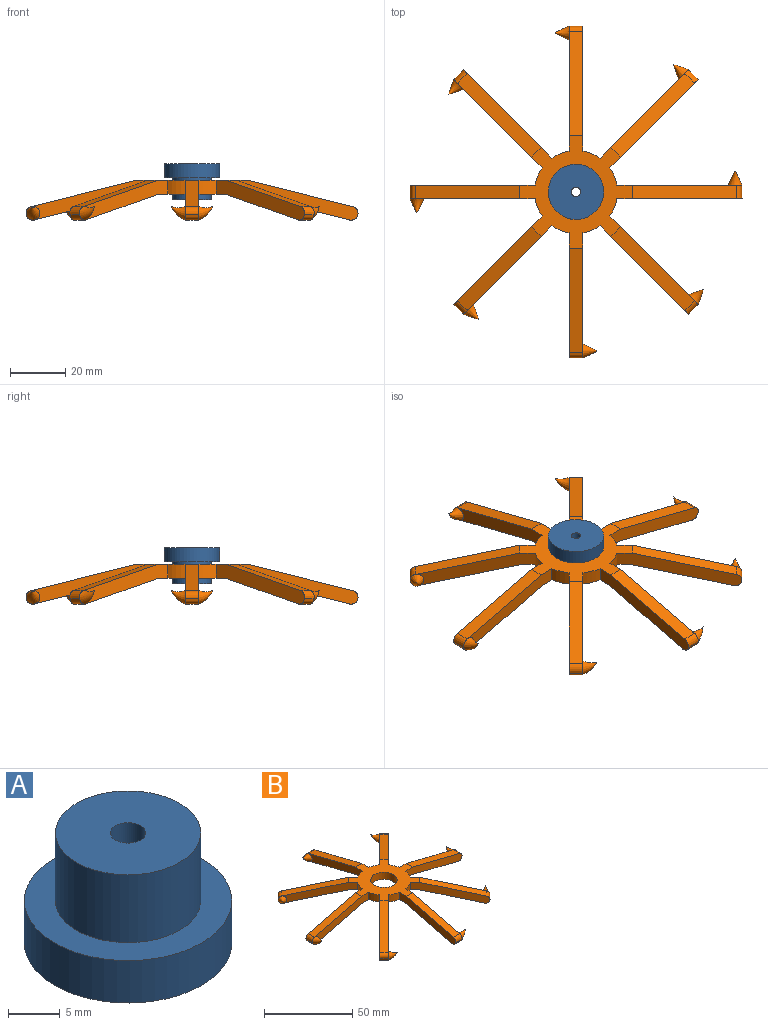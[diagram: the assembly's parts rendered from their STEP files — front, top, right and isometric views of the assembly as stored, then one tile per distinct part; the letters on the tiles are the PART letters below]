
ASSEMBLY  parts=2 mates=1
PART A: 6 faces, bbox 20x20x13 mm
  f0: cylinder r=10mm len=20mm, axis (0,0,-1), area 314.2mm2, adj f1,f2
  f1: plane 20x20mm, normal (0,0,1), area 160.2mm2, adj f0,f3
  f2: plane 20x20mm, normal (0,0,-1), area 305.1mm2, adj f0,f5
  f3: cylinder r=7mm len=14mm, axis (0,0,-1), area 351.9mm2, adj f1,f4
  f4: plane 14x14mm, normal (0,0,1), area 144.9mm2, adj f3,f5
  f5: cylinder r=1.7mm len=13mm, axis (0,0,-1), area 138.9mm2, adj f2,f4
PART B: 67 faces, bbox 120.2x120.2x14.4 mm
  f0: plane 45.28x14.39mm, normal (0,-1,0), area 229.5mm2, adj f2,f3,f4,f5,f7,f8,f10
  f1: plane 43.39x14.32mm, normal (0,1,0), area 209.9mm2, adj f2,f3,f4,f5,f6,f18
  f2: plane 37.88x9.47mm, normal (0.24,0,0.97), area 195.2mm2, adj f0,f1,f5,f8
  f3: plane 37.28x9.32mm, normal (-0.24,0,-0.97), area 192.1mm2, adj f0,f1,f4,f7
  f4: plane 39.38x39.38mm, normal (0,0,-1), area 720.6mm2, adj f0,f1,f3,f9,f10,f11,f12,f14
  f5: plane 40.62x40.62mm, normal (0,0,1), area 745.2mm2, adj f0,f1,f2,f9,f10,f11,f12,f13
  f6: bspline ~5x5mm, area 48.7mm2, adj f1,f7,f8
  f7: extruded ~5x3.03mm, area 19.6mm2, adj f0,f3,f6,f8
  f8: extruded ~5x3.03mm, area 19.6mm2, adj f0,f2,f6,f7
  f9: cylinder r=7.5mm len=15mm, axis (0,0,1), area 235.6mm2, adj f4,f5
  f10: cylinder r=15mm len=6.19mm, axis (0,0,1), area 33.8mm2, adj f0,f4,f5,f60
  f11: plane 32.02x32.02mm, normal (0.71,-0.71,0), area 229.5mm2, adj f4,f5,f13,f14,f16,f17,f18
  f12: plane 30.68x30.68mm, normal (-0.71,0.71,0), area 209.9mm2, adj f4,f5,f13,f14,f15,f26
  f13: plane 30.32x30.32mm, normal (0.17,0.17,0.97), area 195.2mm2, adj f5,f11,f12,f17
  f14: plane 29.9x29.89mm, normal (-0.17,-0.17,-0.97), area 192.1mm2, adj f4,f11,f12,f16
  f15: bspline ~5.3x5.3mm, area 48.7mm2, adj f12,f16,f17
  f16: extruded ~5.68x5.68mm, area 19.6mm2, adj f11,f14,f15,f17
  f17: extruded ~4.87x4.87mm, area 19.6mm2, adj f11,f13,f15,f16
  f18: cylinder r=15mm len=6.19mm, axis (0,0,1), area 33.8mm2, adj f1,f4,f5,f11
  f19: plane 45.28x14.39mm, normal (1,0,0), area 229.5mm2, adj f4,f5,f21,f22,f24,f25,f26
  f20: plane 43.39x14.32mm, normal (-1,0,0), area 209.9mm2, adj f4,f5,f21,f22,f23,f34
  f21: plane 37.88x9.47mm, normal (0,0.24,0.97), area 195.2mm2, adj f5,f19,f20,f25
  f22: plane 37.28x9.32mm, normal (0,-0.24,-0.97), area 192.1mm2, adj f4,f19,f20,f24
  f23: bspline ~5x5mm, area 48.7mm2, adj f20,f24,f25
  f24: extruded ~5x3.03mm, area 19.6mm2, adj f19,f22,f23,f25
  f25: extruded ~5x3.03mm, area 19.6mm2, adj f19,f21,f23,f24
  f26: cylinder r=15mm len=6.19mm, axis (0,0,1), area 33.8mm2, adj f4,f5,f12,f19
  f27: plane 32.02x32.02mm, normal (0.71,0.71,0), area 229.5mm2, adj f4,f5,f29,f30,f32,f33,f34
  f28: plane 30.68x30.68mm, normal (-0.71,-0.71,0), area 209.9mm2, adj f4,f5,f29,f30,f31,f42
  f29: plane 30.32x30.32mm, normal (-0.17,0.17,0.97), area 195.2mm2, adj f5,f27,f28,f33
  f30: plane 29.9x29.89mm, normal (0.17,-0.17,-0.97), area 192.1mm2, adj f4,f27,f28,f32
  f31: bspline ~5.3x5.3mm, area 48.7mm2, adj f28,f32,f33
  f32: extruded ~5.68x5.68mm, area 19.6mm2, adj f27,f30,f31,f33
  f33: extruded ~4.87x4.87mm, area 19.6mm2, adj f27,f29,f31,f32
  f34: cylinder r=15mm len=6.19mm, axis (0,0,1), area 33.8mm2, adj f4,f5,f20,f27
  f35: plane 45.28x14.39mm, normal (0,1,0), area 229.5mm2, adj f4,f5,f37,f38,f40,f41,f42
  f36: plane 43.39x14.32mm, normal (0,-1,0), area 209.9mm2, adj f4,f5,f37,f38,f39,f50
  f37: plane 37.88x9.47mm, normal (-0.24,0,0.97), area 195.2mm2, adj f5,f35,f36,f41
  f38: plane 37.28x9.32mm, normal (0.24,0,-0.97), area 192.1mm2, adj f4,f35,f36,f40
  f39: bspline ~5x5mm, area 48.7mm2, adj f36,f40,f41
  f40: extruded ~5x3.03mm, area 19.6mm2, adj f35,f38,f39,f41
  f41: extruded ~5x3.03mm, area 19.6mm2, adj f35,f37,f39,f40
  f42: cylinder r=15mm len=6.19mm, axis (0,0,1), area 33.8mm2, adj f4,f5,f28,f35
  f43: plane 32.02x32.02mm, normal (-0.71,0.71,0), area 229.5mm2, adj f4,f5,f45,f46,f48,f49,f50
  f44: plane 30.68x30.68mm, normal (0.71,-0.71,0), area 209.9mm2, adj f4,f5,f45,f46,f47,f58
  f45: plane 30.32x30.32mm, normal (-0.17,-0.17,0.97), area 195.2mm2, adj f5,f43,f44,f49
  f46: plane 29.9x29.89mm, normal (0.17,0.17,-0.97), area 192.1mm2, adj f4,f43,f44,f48
  f47: bspline ~5.3x5.3mm, area 48.7mm2, adj f44,f48,f49
  f48: extruded ~5.68x5.68mm, area 19.6mm2, adj f43,f46,f47,f49
  f49: extruded ~4.87x4.87mm, area 19.6mm2, adj f43,f45,f47,f48
  f50: cylinder r=15mm len=6.19mm, axis (0,0,1), area 33.8mm2, adj f4,f5,f36,f43
  f51: plane 45.28x14.39mm, normal (-1,0,0), area 229.5mm2, adj f4,f5,f53,f54,f56,f57,f58
  f52: plane 43.39x14.32mm, normal (1,0,0), area 209.9mm2, adj f4,f5,f53,f54,f55,f66
  f53: plane 37.88x9.47mm, normal (0,-0.24,0.97), area 195.2mm2, adj f5,f51,f52,f57
  f54: plane 37.28x9.32mm, normal (0,0.24,-0.97), area 192.1mm2, adj f4,f51,f52,f56
  f55: bspline ~5x5mm, area 48.7mm2, adj f52,f56,f57
  f56: extruded ~5x3.03mm, area 19.6mm2, adj f51,f54,f55,f57
  f57: extruded ~5x3.03mm, area 19.6mm2, adj f51,f53,f55,f56
  f58: cylinder r=15mm len=6.19mm, axis (0,0,1), area 33.8mm2, adj f4,f5,f44,f51
  f59: plane 32.02x32.02mm, normal (-0.71,-0.71,0), area 229.5mm2, adj f4,f5,f61,f62,f64,f65,f66
  f60: plane 30.68x30.68mm, normal (0.71,0.71,0), area 209.9mm2, adj f4,f5,f10,f61,f62,f63
  f61: plane 30.32x30.32mm, normal (0.17,-0.17,0.97), area 195.2mm2, adj f5,f59,f60,f65
  f62: plane 29.9x29.89mm, normal (-0.17,0.17,-0.97), area 192.1mm2, adj f4,f59,f60,f64
  f63: bspline ~5.3x5.3mm, area 48.7mm2, adj f60,f64,f65
  f64: extruded ~5.68x5.68mm, area 19.6mm2, adj f59,f62,f63,f65
  f65: extruded ~4.87x4.87mm, area 19.6mm2, adj f59,f61,f63,f64
  f66: cylinder r=15mm len=6.19mm, axis (0,0,1), area 33.8mm2, adj f4,f5,f52,f59
PLACE A rot(axis=(1,0,0),180deg) t=(0,0,6)mm
PLACE B t=(0,0,-2.5)mm
MATE fastened B.f9 <-> A.f0  axis (0,0,1) through (0,0,0)mm
